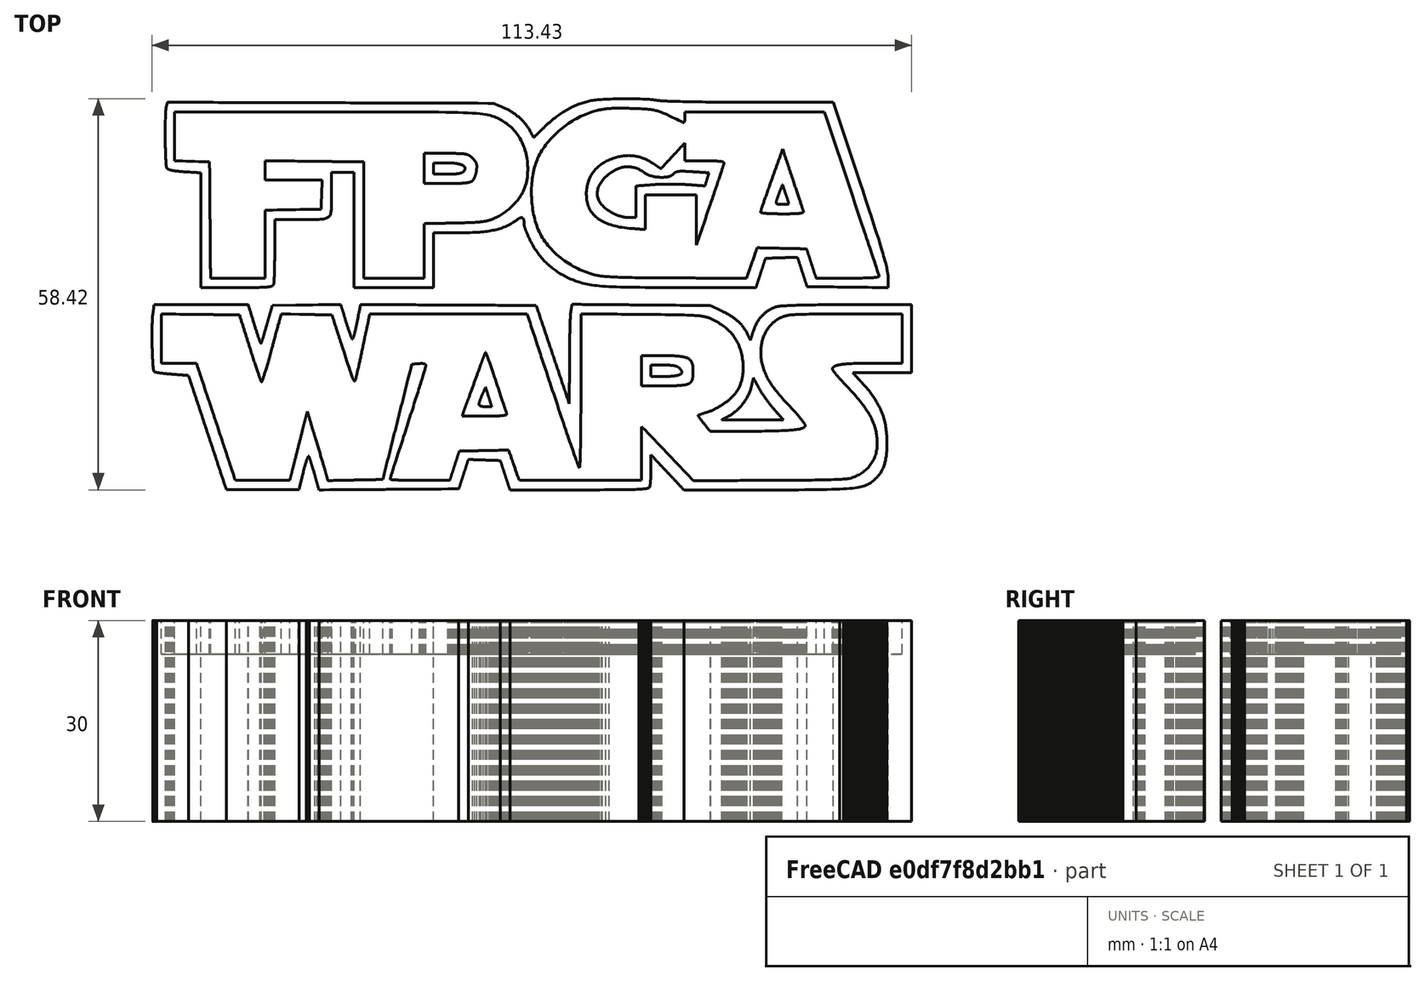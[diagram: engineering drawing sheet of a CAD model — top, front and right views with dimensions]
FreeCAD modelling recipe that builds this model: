
FCSTD DOCUMENT  (FreeCAD 0.16R6707 (Git))
Label: dxf_fpgawarsstarwarsnonofficiallogo
License: All rights reserved
LicenseURL: http://en.wikipedia.org/wiki/All_rights_reserved
objects: Part::Feature×18, Part::Extrusion×16, Part::Cut×11, Part::MultiFuse×3, App::DocumentObjectGroup×2
note: 48 computed .brp shape members not serialized (recipe doc carries the construction recipe); baked Part::Feature solids carry a one-line shape summary decoded from their .brp

FEATURE [Part::Extrusion] Extrude_Polyline001  label="wars_outside"
  Dir = (0,0,30)
  Solid = true
FEATURE [Part::Extrusion] Extrude_Polyline002  label="wars_inside"
  Dir = (0,0,15)
  Solid = true
FEATURE [Part::Extrusion] Extrude_Polyline003  label="Polyline003_Extrude"
  Dir = (0,0,20)
  Solid = false
FEATURE [Part::Extrusion] Extrude_Polyline004  label="Polyline004_Extrude"
  Dir = (0,0,25)
  Solid = true
FEATURE [Part::Cut] Cut
  Base = -> Extrude_Polyline003
  Tool = -> Extrude_Polyline004
FEATURE [Part::Cut] Cut001
  Base = -> Extrude_Polyline002
  Tool = -> Cut
FEATURE [Part::Extrusion] Extrude_Polyline005  label="Polyline005_Extrude"
  Dir = (0,0,20)
  Solid = true
FEATURE [Part::Extrusion] Extrude_Polyline006  label="Polyline006_Extrude"
  Dir = (0,0,25)
  Solid = true
FEATURE [Part::Cut] Cut002
  Base = -> Extrude_Polyline005
  Tool = -> Extrude_Polyline006
FEATURE [Part::Extrusion] Extrude_Polyline008  label="FPGA_outside"
  Dir = (0,0,30)
  Solid = true
FEATURE [Part::Extrusion] Extrude_Polyline009  label="Polyline009_Extrude"
  Dir = (0,0,15)
  Solid = true
FEATURE [Part::Extrusion] Extrude_Polyline010  label="Polyline010_Extrude"
  Dir = (0,0,20)
  Solid = true
FEATURE [Part::Extrusion] Extrude_Polyline011  label="Polyline011_Extrude"
  Dir = (0,0,25)
  Solid = true
FEATURE [Part::Cut] Cut004
  Base = -> Extrude_Polyline010
  Tool = -> Extrude_Polyline011
FEATURE [Part::Cut] Cut005  label="fp_inside"
  Base = -> Extrude_Polyline009
  Tool = -> Cut004
FEATURE [Part::Extrusion] Extrude_Polyline012  label="GA_inside"
  Dir = (0,0,15)
  Solid = true
FEATURE [Part::Extrusion] Extrude_Polyline013  label="Polyline013_Extrude"
  Dir = (0,0,20)
  Solid = true
FEATURE [Part::Extrusion] Extrude_Polyline014  label="Polyline014_Extrude"
  Dir = (0,0,25)
  Solid = true
FEATURE [Part::Cut] Cut006
  Base = -> Extrude_Polyline013
  Tool = -> Extrude_Polyline014
FEATURE [Part::Extrusion] Extrude_Polyline015  label="Polyline015_Extrude"
  Dir = (0,0,20)
  Solid = true
FEATURE [Part::Extrusion] Extrude_Polyline016  label="Polyline016_Extrude"
  Dir = (0,0,25)
  Solid = true
FEATURE [Part::Cut] Cut007
  Base = -> Extrude_Polyline015
  Tool = -> Extrude_Polyline016
FEATURE [Part::MultiFuse] Fusion
  Shapes = -> [Cut006,Cut007]
FEATURE [Part::Cut] Cut008  label="GA_inside001"
  Base = -> Extrude_Polyline012
  Tool = -> Fusion
FEATURE [Part::MultiFuse] Fusion001  label="FPGA_inside"
  Placement = pos=(0,0,25) rot=(0,0,1;0rad)
  Shapes = -> [Cut005,Cut008]
FEATURE [Part::Cut] Cut009  label="FPGA"
  Base = -> Extrude_Polyline008
  Tool = -> Fusion001
FEATURE [Part::Feature] Polyline
  shape: bbox 123.9 x 62.65 x 2e-07 mm, 1 faces, 0 solids (baked)
FEATURE [Part::Feature] Polyline001
  shape: bbox 113.4 x 27.72 x 2e-07 mm, 1 faces, 0 solids (baked)
FEATURE [Part::Feature] Polyline002
  shape: bbox 110.6 x 24.9 x 2e-07 mm, 1 faces, 0 solids (baked)
FEATURE [Part::Feature] Polyline003
  shape: bbox 6.688 x 9.543 x 2e-07 mm, 1 faces, 0 solids (baked)
FEATURE [Part::Feature] Polyline004
  shape: bbox 1.916 x 2.894 x 2e-07 mm, 1 faces, 0 solids (baked)
FEATURE [Part::Feature] Polyline005
  shape: bbox 7.714 x 4.516 x 2e-07 mm, 1 faces, 0 solids (baked)
FEATURE [Part::Feature] Polyline006
  shape: bbox 4.617 x 1.693 x 2e-07 mm, 1 faces, 0 solids (baked)
FEATURE [Part::Feature] Polyline007
  shape: bbox 9.217 x 6.278 x 2e-07 mm, 1 faces, 0 solids (baked)
FEATURE [Part::Feature] Polyline008
  shape: bbox 108 x 28.2 x 2e-07 mm, 1 faces, 0 solids (baked)
FEATURE [Part::Feature] Polyline009
  shape: bbox 52.74 x 24.84 x 2e-07 mm, 1 faces, 0 solids (baked)
FEATURE [Part::Feature] Polyline010
  shape: bbox 7.868 x 4.516 x 2e-07 mm, 1 faces, 0 solids (baked)
FEATURE [Part::Feature] Polyline011
  shape: bbox 4.724 x 1.693 x 2e-07 mm, 1 faces, 0 solids (baked)
FEATURE [Part::Feature] Polyline012
  shape: bbox 51.92 x 25.38 x 2e-07 mm, 1 faces, 0 solids (baked)
FEATURE [Part::Feature] Polyline013
  shape: bbox 20.55 x 15.24 x 2e-07 mm, 1 faces, 0 solids (baked)
FEATURE [Part::Feature] Polyline014
  shape: bbox 16.69 x 7.602 x 2e-07 mm, 1 faces, 0 solids (baked)
FEATURE [Part::Feature] Polyline015
  shape: bbox 6.43 x 9.673 x 2e-07 mm, 1 faces, 0 solids (baked)
FEATURE [Part::Feature] Polyline016
  shape: bbox 1.895 x 2.962 x 2e-07 mm, 1 faces, 0 solids (baked)
FEATURE [App::DocumentObjectGroup] _  label="0"
  Group = -> [Polyline,Polyline001,Polyline002,Polyline003,Polyline004,Polyline005,Polyline006,Polyline007,Polyline008,Polyline009,Polyline010,Polyline011,Polyline012,Polyline013,Polyline014,Polyline015,Polyline016]
FEATURE [App::DocumentObjectGroup] fpgawarsstarwarslogo  label="logo_dxf"
  Group = -> [_]
FEATURE [Part::Feature] Polyline017
  shape: bbox 9.217 x 6.278 x 2e-07 mm, 1 faces, 0 solids (baked)
FEATURE [Part::Cut] Cut003  label="wars_inside001"
  Base = -> Cut001
  Placement = pos=(0,0,25) rot=(0,0,1;0rad)
  Tool = -> Cut002
FEATURE [Part::Extrusion] Extrude_Polyline017  label="Polyline017_Extrude"
  Base = -> Polyline017
  Dir = (0,0,15)
  Placement = pos=(0,0,25) rot=(0,0,1;0rad)
  Solid = true
FEATURE [Part::MultiFuse] Fusion002  label="WARS_inside"
  Shapes = -> [Cut003,Extrude_Polyline017]
FEATURE [Part::Cut] Cut010  label="WARS"
  Base = -> Extrude_Polyline001
  Tool = -> Fusion002
